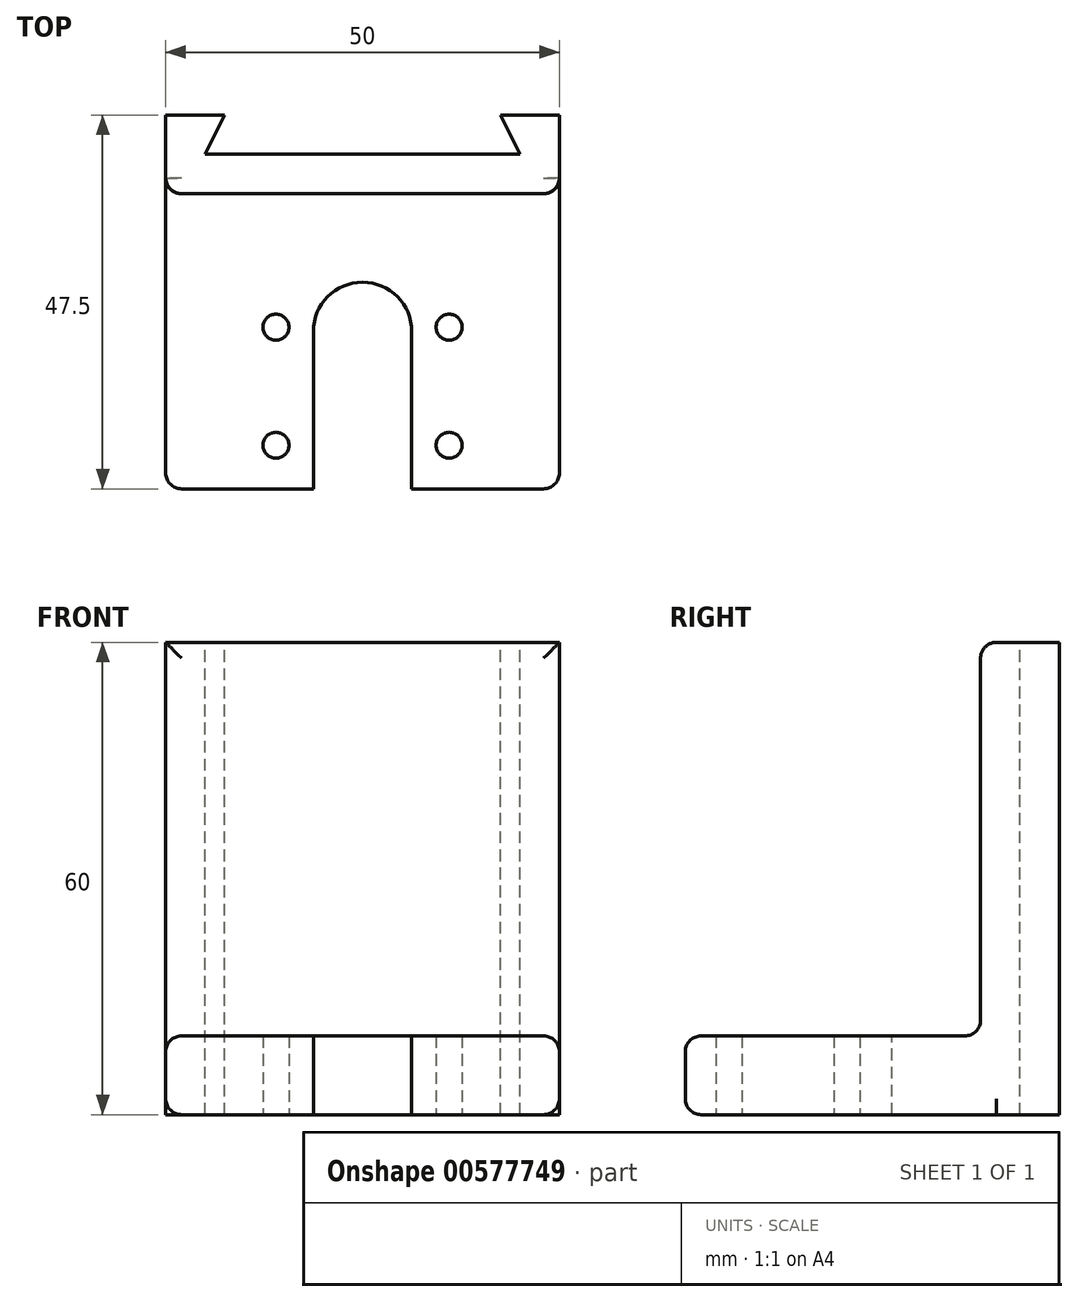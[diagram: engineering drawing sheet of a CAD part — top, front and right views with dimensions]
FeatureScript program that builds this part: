
annotation { "Feature Type Name" : "Feature", "Feature Type Description" : "" }
export const myFeature = defineFeature(function(context is Context, id is Id, definition is map)
    precondition{}
    {
        {
            var Q0;
            Q0=qCreatedBy(makeId("Right.planeOp"),FACE);
            var sketch = newSketch(context, id + "F0", { "sketchPlane" : qUnion([Q0])});
            skLineSegment(sketch, "E0.bottom", {"start": v(2.5, 30) * mm, "end": v(-2.5, 30) * mm});
            skLineSegment(sketch, "E0.top", {"start": v(2.5, -30) * mm, "end": v(-2.5, -30) * mm});
            skLineSegment(sketch, "E0.left", {"start": v(2.5, 30) * mm, "end": v(2.5, -30) * mm});
            skLineSegment(sketch, "E0.right", {"start": v(-2.5, 30) * mm, "end": v(-2.5, -30) * mm});
            skSolve(sketch);
        }
        {
            var Q0;
            Q0=makeQuery(id+"F0.imprint","IMPRINT",FACE,{"disambiguationData":[TD([[makeQuery(id+"F0.imprint","IMPRINT",EDGE,{"derivedFrom":sQuery(id+"F0.wireOp",EDGE,"E0.bottom")}),1.0]])]});
            extrude(context, id + "F1", {"entities" : qUnion([Q0]), "depth" : 25 * mm, "offsetDistance" : 25 * mm, "hasSecondDirection" : true, "secondDirectionOppositeDirection" : true, "secondDirectionDepth" : 25 * mm});
        }
        {
            var Q0;
            Q0=qCreatedBy(makeId("Front.planeOp"),FACE);
            var sketch = newSketch(context, id + "F2", { "sketchPlane" : qUnion([Q0])});
            skLineSegment(sketch, "E1", {"start": v(-25, -20) * mm, "end": v(25, -20) * mm});
            skLineSegment(sketch, "E2", {"start": v(25, -20) * mm, "end": v(25, -30) * mm});
            skLineSegment(sketch, "E3", {"start": v(25, -30) * mm, "end": v(-25, -30) * mm});
            skLineSegment(sketch, "E4", {"start": v(-25, -30) * mm, "end": v(-25, -20) * mm});
            skSolve(sketch);
        }
        {
            var Q0;
            Q0 = qSketchRegion(id + "F2", true);
            extrude(context, id + "F3", {"entities" : qUnion([Q0]), "operationType" : NewBodyOperationType.ADD, "depth" : 40 * mm, "offsetDistance" : 25 * mm});
        }
        {
            var Q0;
            Q0=makeQuery(id+"F3.opExtrude","SWEPT_FACE",FACE,{"disambiguationData":[OSD([sQuery(id+"F2.wireOp",EDGE,"E1")])]});
            var sketch = newSketch(context, id + "F4", { "sketchPlane" : qUnion([Q0])});
            skLineSegment(sketch, "E5", {"start": v(-6.25, -20) * mm, "end": v(-6.25, -40) * mm});
            skLineSegment(sketch, "E6", {"start": v(-6.25, -40) * mm, "end": v(6.25, -40) * mm});
            skLineSegment(sketch, "E7", {"start": v(6.25, -40) * mm, "end": v(6.25, -20) * mm});
            skCircle(sketch, "E8", {"center": v(0, -20) * mm, "radius": 6.25 * mm});
            skPoint(sketch, "E8.third.point", {"position": v(0, -26.25) * mm});
            skSolve(sketch);
        }
        {
            var Q0;
            Q0 = qSketchRegion(id + "F4", true);
            extrude(context, id + "F5", {"entities" : qUnion([Q0]), "operationType" : NewBodyOperationType.REMOVE, "oppositeDirection" : true, "depth" : 25 * mm, "offsetDistance" : 25 * mm});
        }
        {
            var Q0;
            Q0=makeQuery(id+"F3.opExtrude","SWEPT_EDGE",EDGE,{"disambiguationData":[OSD([sQuery(id+"F2.wireOp",EDGE,"E1"),sQuery(id+"F2.wireOp",EDGE,"E4")])]});
            var Q1;
            Q1=makeQuery(id+"F1.opExtrude","CAP_EDGE",EDGE,{"disambiguationData":[OSD([sQuery(id+"F0.wireOp",EDGE,"E0.right")])],"isStart":true});
            var Q2;
            Q2=makeQuery(id+"F3.opExtrude","SWEPT_EDGE",EDGE,{"disambiguationData":[OSD([sQuery(id+"F2.wireOp",EDGE,"E1"),sQuery(id+"F2.wireOp",EDGE,"E2")])]});
            var Q3;
            Q3=makeQuery(id+"F1.opExtrude","CAP_EDGE",EDGE,{"disambiguationData":[OSD([sQuery(id+"F0.wireOp",EDGE,"E0.right")])],"isStart":false});
            var Q4;
            {var subQ0=sQuery(id+"F2.wireOp",EDGE,"E4");var subQ1=sQuery(id+"F2.wireOp",EDGE,"E1");Q4=makeQuery(id+"F5.boolean.opBoolean","SPLIT",EDGE,{"disambiguationData":[TD([makeQuery(id+"F3.opExtrude","SWEPT_FACE",FACE,{"disambiguationData":[OSD([subQ0])]})])],"derivedFrom":makeQuery(id+"F3.opExtrude","CAP_EDGE",EDGE,{"disambiguationData":[OSD([subQ1])],"isStart":false})});}
            var Q5;
            {var subQ0=sQuery(id+"F2.wireOp",EDGE,"E2");var subQ1=sQuery(id+"F2.wireOp",EDGE,"E1");Q5=makeQuery(id+"F5.boolean.opBoolean","SPLIT",EDGE,{"disambiguationData":[TD([makeQuery(id+"F3.opExtrude","SWEPT_FACE",FACE,{"disambiguationData":[OSD([subQ0])]})])],"derivedFrom":makeQuery(id+"F3.opExtrude","CAP_EDGE",EDGE,{"disambiguationData":[OSD([subQ1])],"isStart":false})});}
            var Q6;
            {var subQ0=sQuery(id+"F2.wireOp",EDGE,"E3");var subQ1=sQuery(id+"F2.wireOp",EDGE,"E4");Q6=makeQuery(id+"F5.boolean.opBoolean","SPLIT",EDGE,{"disambiguationData":[TD([makeQuery(id+"F3.opExtrude","SWEPT_FACE",FACE,{"disambiguationData":[OSD([subQ1])]})])],"derivedFrom":makeQuery(id+"F3.opExtrude","CAP_EDGE",EDGE,{"disambiguationData":[OSD([subQ0])],"isStart":false})});}
            var Q7;
            Q7=makeQuery(id+"F3.boolean.opBoolean","MERGE",EDGE,{"derivedFrom":[makeQuery(id+"F1.opExtrude","CAP_EDGE",EDGE,{"disambiguationData":[OSD([sQuery(id+"F0.wireOp",EDGE,"E0.top")])],"isStart":true}),makeQuery(id+"F3.opExtrude","SWEPT_EDGE",EDGE,{"disambiguationData":[OSD([sQuery(id+"F2.wireOp",EDGE,"E3"),sQuery(id+"F2.wireOp",EDGE,"E4")])]})]});
            var Q8;
            Q8=makeQuery(id+"F3.boolean.opBoolean","MERGE",EDGE,{"derivedFrom":[makeQuery(id+"F1.opExtrude","CAP_EDGE",EDGE,{"disambiguationData":[OSD([sQuery(id+"F0.wireOp",EDGE,"E0.top")])],"isStart":false}),makeQuery(id+"F3.opExtrude","SWEPT_EDGE",EDGE,{"disambiguationData":[OSD([sQuery(id+"F2.wireOp",EDGE,"E2"),sQuery(id+"F2.wireOp",EDGE,"E3")])]})]});
            var Q9;
            {var subQ0=sQuery(id+"F2.wireOp",EDGE,"E2");var subQ1=sQuery(id+"F2.wireOp",EDGE,"E3");Q9=makeQuery(id+"F5.boolean.opBoolean","SPLIT",EDGE,{"disambiguationData":[TD([makeQuery(id+"F3.opExtrude","SWEPT_FACE",FACE,{"disambiguationData":[OSD([subQ0])]})])],"derivedFrom":makeQuery(id+"F3.opExtrude","CAP_EDGE",EDGE,{"disambiguationData":[OSD([subQ1])],"isStart":false})});}
            var Q10;
            Q10=makeQuery(id+"F3.opExtrude","CAP_EDGE",EDGE,{"disambiguationData":[OSD([sQuery(id+"F2.wireOp",EDGE,"E2")])],"isStart":false});
            var Q11;
            Q11=makeQuery(id+"F3.opExtrude","CAP_EDGE",EDGE,{"disambiguationData":[OSD([sQuery(id+"F2.wireOp",EDGE,"E4")])],"isStart":false});
            var Q12;
            Q12=makeQuery(id+"F1.opExtrude","SWEPT_EDGE",EDGE,{"disambiguationData":[OSD([sQuery(id+"F0.wireOp",EDGE,"E0.bottom"),sQuery(id+"F0.wireOp",EDGE,"E0.right")])]});
            var Q13;
            Q13=makeQuery(id+"F3.boolean.opBoolean","INTERSECT",EDGE,{"derivedFrom":[makeQuery(id+"F1.opExtrude","SWEPT_FACE",FACE,{"disambiguationData":[OSD([sQuery(id+"F0.wireOp",EDGE,"E0.right")])]}),makeQuery(id+"F3.opExtrude","SWEPT_FACE",FACE,{"disambiguationData":[OSD([sQuery(id+"F2.wireOp",EDGE,"E1")])]})]});
            fillet(context, id + "F6", {"entities" : qUnion([Q0, Q1, Q2, Q3, Q4, Q5, Q6, Q7, Q8, Q9, Q10, Q11, Q12, Q13]), "radius" : 2 * mm, "tangentPropagation" : true, "allowEdgeOverflow" : false});
        }
        {
            var Q0;
            Q0=makeQuery(id+"F3.opExtrude","SWEPT_FACE",FACE,{"disambiguationData":[OSD([sQuery(id+"F2.wireOp",EDGE,"E1")])]});
            var sketch = newSketch(context, id + "F7", { "sketchPlane" : qUnion([Q0])});
            skPoint(sketch, "E9", {"position": v(0, -25) * mm});
            skLineSegment(sketch, "E10.bottom", {"start": v(-11, -19.46) * mm, "end": v(11, -19.46) * mm, "construction": true});
            skLineSegment(sketch, "E10.top", {"start": v(-11, -34.46) * mm, "end": v(11, -34.46) * mm, "construction": true});
            skLineSegment(sketch, "E10.left", {"start": v(-11, -19.46) * mm, "end": v(-11, -34.46) * mm, "construction": true});
            skLineSegment(sketch, "E10.right", {"start": v(11, -19.46) * mm, "end": v(11, -34.46) * mm, "construction": true});
            skSolve(sketch);
        }
        {
            var Q0;
            Q0=sQuery(id+"F7.wireOp",VERTEX,"E10.bottom.start");
            var Q1;
            Q1=sQuery(id+"F7.wireOp",VERTEX,"E10.bottom.end");
            var Q2;
            Q2=sQuery(id+"F7.wireOp",VERTEX,"E10.right.end");
            var Q3;
            Q3=sQuery(id+"F7.wireOp",VERTEX,"E10.left.end");
            var Q4;
            Q4=makeQuery(id+"F1.opExtrude","SWEPT_BODY",BODY,{"disambiguationData":[OSD([sQuery(id+"F0.wireOp",EDGE,"E0.bottom"),sQuery(id+"F0.wireOp",EDGE,"E0.top"),sQuery(id+"F0.wireOp",EDGE,"E0.left"),sQuery(id+"F0.wireOp",EDGE,"E0.right")])]});
            hole(context, id + "F8", {"style" : HoleStyle.SIMPLE, "endStyle" : HoleEndStyle.THROUGH, "standardTappedOrClearance" : lookupTablePath({ "standard" : "ISO", "fit" : "Normal", "size" : "M3", "type" : "Clearance" }), "standardBlindInLast" : lookupTablePath({ "fit" : "Standard", "standard" : "ISO", "size" : "M3", "type" : "Clearance" }), "holeDiameter" : 3.3 * mm, "majorDiameter" : 5 * mm, "isTappedThrough" : true, "tappedDepth" : 12 * mm, "tapClearance" : 3, "startFromSketch" : true, "locations" : qUnion([Q0, Q1, Q2, Q3]), "scope" : qUnion([Q4])});
        }
        {
            var Q0;
            Q0=makeQuery(id+"F1.opExtrude","SWEPT_FACE",FACE,{"disambiguationData":[OSD([sQuery(id+"F0.wireOp",EDGE,"E0.bottom")])]});
            var sketch = newSketch(context, id + "F9", { "sketchPlane" : qUnion([Q0])});
            skLineSegment(sketch, "E11", {"start": v(-25, -0.5) * mm, "end": v(25, -0.5) * mm});
            skLineSegment(sketch, "E12", {"start": v(25, -0.5) * mm, "end": v(25, 7.5) * mm});
            skLineSegment(sketch, "E13", {"start": v(25, 7.5) * mm, "end": v(17.5, 7.5) * mm});
            skLineSegment(sketch, "E14", {"start": v(17.5, 7.5) * mm, "end": v(20, 2.5) * mm});
            skLineSegment(sketch, "E15", {"start": v(20, 2.5) * mm, "end": v(20, 2.5) * mm});
            skLineSegment(sketch, "E16", {"start": v(20, 2.5) * mm, "end": v(-20, 2.5) * mm});
            skLineSegment(sketch, "E17", {"start": v(-20, 2.5) * mm, "end": v(-20, 2.5) * mm});
            skLineSegment(sketch, "E18", {"start": v(-20, 2.5) * mm, "end": v(-17.5, 7.5) * mm});
            skLineSegment(sketch, "E19", {"start": v(-17.5, 7.5) * mm, "end": v(-25, 7.5) * mm});
            skLineSegment(sketch, "E20", {"start": v(-25, 7.5) * mm, "end": v(-25, -0.5) * mm});
            skSolve(sketch);
        }
        {
            var Q0;
            Q0 = qSketchRegion(id + "F9", true);
            var Q1;
            Q1=qCreatedBy(makeId("Top.planeOp"),FACE);
            extrude(context, id + "F10", {"entities" : qUnion([Q0]), "operationType" : NewBodyOperationType.ADD, "oppositeDirection" : true, "depth" : 60 * mm, "endBoundEntityFace" : qUnion([Q1]), "offsetDistance" : 25 * mm});
        }
    });
